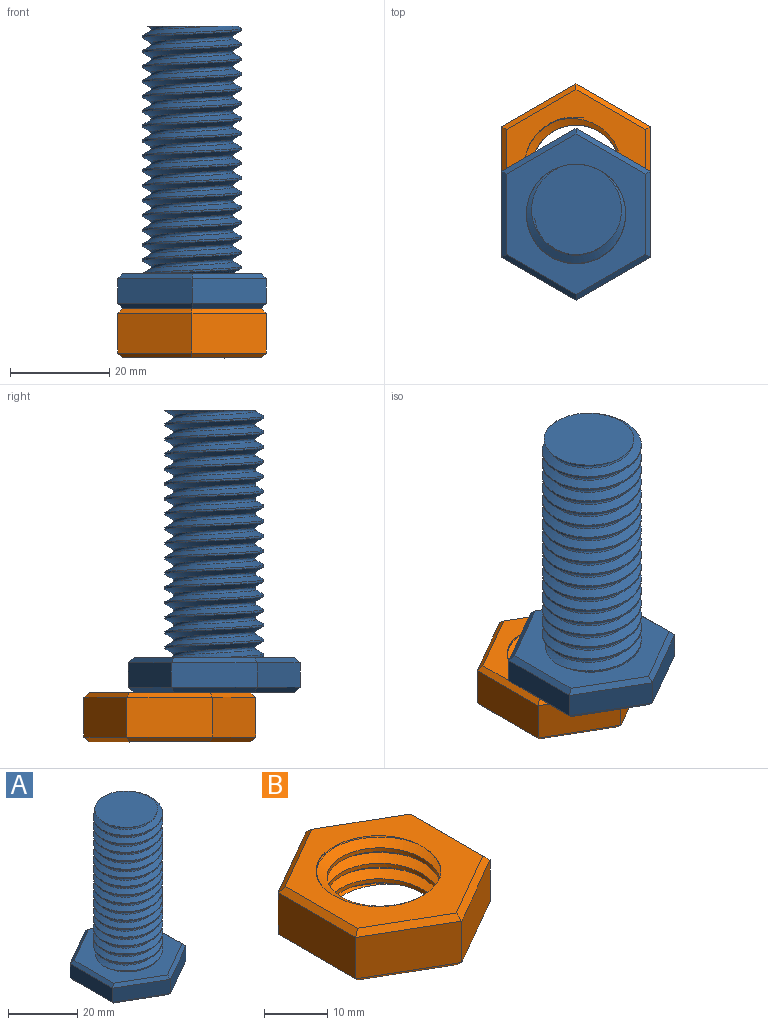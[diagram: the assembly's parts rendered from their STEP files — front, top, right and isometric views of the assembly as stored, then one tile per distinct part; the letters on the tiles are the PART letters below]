
ASSEMBLY  parts=2 mates=1
PART A: 25 faces, bbox 30.8x35.5x59 mm
  f0: plane 15x8.66mm, normal (0.5,-0.87,0), area 86.6mm2, adj f1,f5,f13,f23
  f1: plane 17.32x5mm, normal (1,0,0), area 86.6mm2, adj f0,f2,f14,f21
  f2: plane 15x8.66mm, normal (0.5,0.87,0), area 86.6mm2, adj f1,f3,f16,f19
  f3: plane 15x8.66mm, normal (-0.5,0.87,0), area 86.6mm2, adj f2,f4,f18,f20
  f4: plane 17.32x5mm, normal (-1,0,0), area 86.6mm2, adj f3,f5,f17,f22
  f5: plane 15x8.66mm, normal (-0.5,-0.87,0), area 86.6mm2, adj f0,f4,f15,f24
  f6: plane 33.17x28.84mm, normal (0,0,1), area 419.8mm2, adj f8,f10,f11,f12,f13,f14,f15,f16
  f7: plane 32.33x28mm, normal (0,0,-1), area 679mm2, adj f19,f20,f21,f22,f23,f24
  f8: cylinder r=10mm len=50mm, axis (0,0,-1), area 537.9mm2, adj f6,f9,f11,f12
  f9: plane 19.06x18.96mm, normal (0,0,1), area 259.1mm2, adj f8,f10,f11,f12
  f10: bspline ~52.25x19.34mm, area 728.2mm2, adj f6,f9,f11,f12
  f11: bspline ~52.44x23.09mm, area 1806.7mm2, adj f6,f8,f9,f10
  f12: bspline ~51.94x23.09mm, area 1804.3mm2, adj f6,f8,f9,f10
  f13: plane 15x9.24mm, normal (0.35,-0.61,0.71), area 23.7mm2, adj f0,f6,f14,f15
  f14: plane 17.32x1mm, normal (0.71,0,0.71), area 23.7mm2, adj f1,f6,f13,f16
  f15: plane 15x9.24mm, normal (-0.35,-0.61,0.71), area 23.7mm2, adj f5,f6,f13,f17
  f16: plane 15x9.24mm, normal (0.35,0.61,0.71), area 23.7mm2, adj f2,f6,f14,f18
  f17: plane 17.32x1mm, normal (-0.71,0,0.71), area 23.7mm2, adj f4,f6,f15,f18
  f18: plane 15x9.24mm, normal (-0.35,0.61,0.71), area 23.7mm2, adj f3,f6,f16,f17
  f19: plane 15x9.24mm, normal (0.35,0.61,-0.71), area 23.7mm2, adj f2,f7,f20,f21
  f20: plane 15x9.24mm, normal (-0.35,0.61,-0.71), area 23.7mm2, adj f3,f7,f19,f22
  f21: plane 17.32x1mm, normal (0.71,0,-0.71), area 23.7mm2, adj f1,f7,f19,f23
  f22: plane 17.32x1mm, normal (-0.71,0,-0.71), area 23.7mm2, adj f4,f7,f20,f24
  f23: plane 15x9.24mm, normal (0.35,-0.61,-0.71), area 23.7mm2, adj f0,f7,f21,f24
  f24: plane 15x9.24mm, normal (-0.35,-0.61,-0.71), area 23.7mm2, adj f5,f7,f22,f23
PART B: 24 faces, bbox 30.9x35.5x13.5 mm
  f0: plane 33.22x28.89mm, normal (0,0,1), area 381mm2, adj f8,f9,f10,f11,f18,f19,f20,f21
  f1: plane 33.22x28.89mm, normal (0,0,-1), area 381mm2, adj f8,f9,f10,f11,f12,f13,f14,f15
  f2: plane 15x8.66mm, normal (0.5,-0.87,0), area 138.6mm2, adj f3,f7,f15,f22
  f3: plane 17.32x8mm, normal (1,0,0), area 138.6mm2, adj f2,f4,f17,f20
  f4: plane 15x8.66mm, normal (0.5,0.87,0), area 138.6mm2, adj f3,f5,f16,f18
  f5: plane 15x8.66mm, normal (-0.5,0.87,0), area 138.6mm2, adj f4,f6,f14,f19
  f6: plane 17.32x8mm, normal (-1,0,0), area 138.6mm2, adj f5,f7,f12,f21
  f7: plane 15x8.66mm, normal (-0.5,-0.87,0), area 138.6mm2, adj f2,f6,f13,f23
  f8: bspline ~24.53x21.25mm, area 384.3mm2, adj f0,f1,f10,f11
  f9: bspline ~24.53x21.25mm, area 385.8mm2, adj f0,f1,f10,f11
  f10: bspline ~24.85x21.52mm, area 97.4mm2, adj f0,f1,f8,f9
  f11: cylinder r=9mm len=18mm, axis (0,0,-1), area 139.3mm2, adj f0,f1,f8,f9
  f12: plane 17.32x1mm, normal (-0.71,0,-0.71), area 23.7mm2, adj f1,f6,f13,f14
  f13: plane 15x9.24mm, normal (-0.35,-0.61,-0.71), area 23.7mm2, adj f1,f7,f12,f15
  f14: plane 15x9.24mm, normal (-0.35,0.61,-0.71), area 23.7mm2, adj f1,f5,f12,f16
  f15: plane 15x9.24mm, normal (0.35,-0.61,-0.71), area 23.7mm2, adj f1,f2,f13,f17
  f16: plane 15x9.24mm, normal (0.35,0.61,-0.71), area 23.7mm2, adj f1,f4,f14,f17
  f17: plane 17.32x1mm, normal (0.71,0,-0.71), area 23.7mm2, adj f1,f3,f15,f16
  f18: plane 15x9.24mm, normal (0.35,0.61,0.71), area 23.7mm2, adj f0,f4,f19,f20
  f19: plane 15x9.24mm, normal (-0.35,0.61,0.71), area 23.7mm2, adj f0,f5,f18,f21
  f20: plane 17.32x1mm, normal (0.71,0,0.71), area 23.7mm2, adj f0,f3,f18,f22
  f21: plane 17.32x1mm, normal (-0.71,0,0.71), area 23.7mm2, adj f0,f6,f19,f23
  f22: plane 15x9.24mm, normal (0.35,-0.61,0.71), area 23.7mm2, adj f0,f2,f20,f23
  f23: plane 15x9.24mm, normal (-0.35,-0.61,0.71), area 23.7mm2, adj f0,f7,f21,f22
PLACE A t=(-47.36,22.76,10)mm
PLACE B at identity
MATE fastened A.f8 <-> B.f0  axis (0,0,-1) through (-47.36,22.76,10)mm
